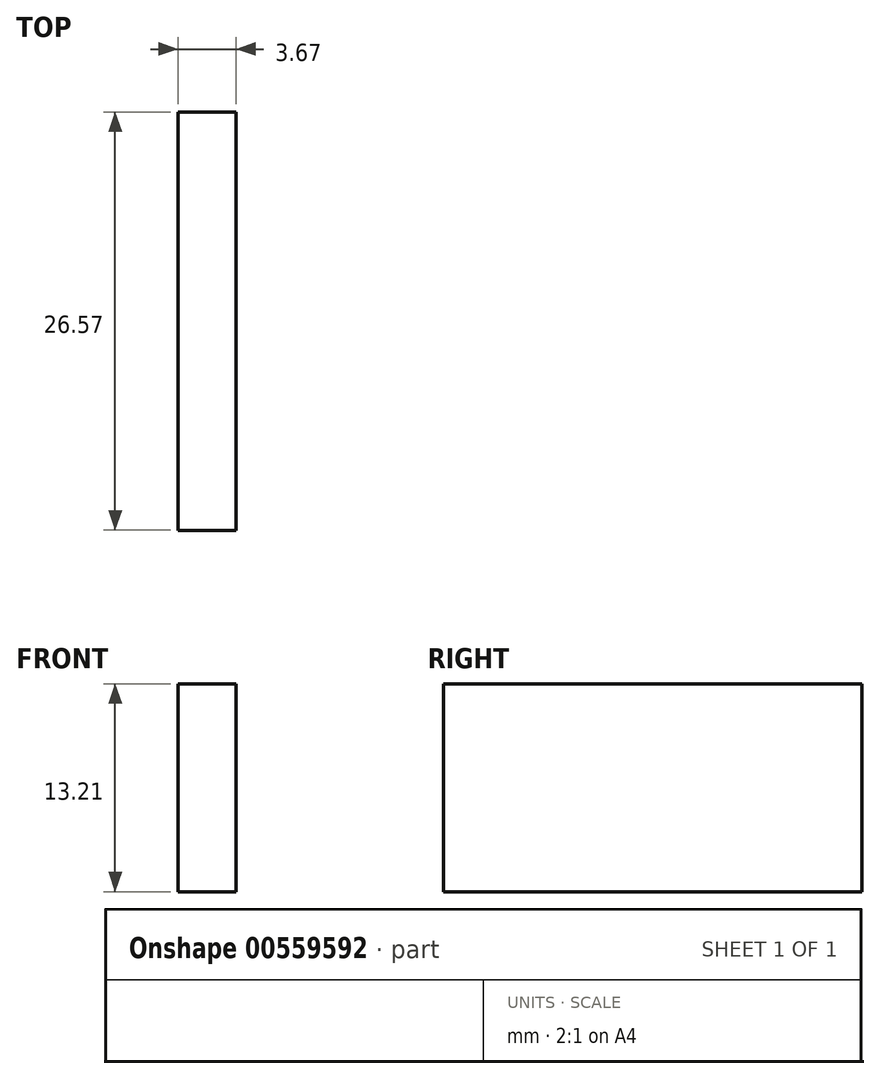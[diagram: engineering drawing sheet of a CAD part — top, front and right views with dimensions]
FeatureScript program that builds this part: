
annotation { "Feature Type Name" : "Feature", "Feature Type Description" : "" }
export const myFeature = defineFeature(function(context is Context, id is Id, definition is map)
    precondition{}
    {
        {
            var Q0;
            Q0=qCreatedBy(makeId("Top.planeOp"),FACE);
            var sketch = newSketch(context, id + "F0", { "sketchPlane" : qUnion([Q0])});
            skLineSegment(sketch, "E0", {"start": v(-37.87, -14.35) * mm, "end": v(-37.87, 12.22) * mm});
            skLineSegment(sketch, "E1", {"start": v(-37.87, 12.22) * mm, "end": v(-34.2, 12.22) * mm});
            skLineSegment(sketch, "E2", {"start": v(-34.2, 12.22) * mm, "end": v(-34.2, -14.35) * mm});
            skLineSegment(sketch, "E3", {"start": v(-34.2, -14.35) * mm, "end": v(-37.87, -14.35) * mm});
            skSolve(sketch);
        }
        {
            var Q0;
            Q0=makeQuery(id+"F0.imprint","IMPRINT",FACE,{"disambiguationData":[TD([[makeQuery(id+"F0.imprint","IMPRINT",EDGE,{"derivedFrom":sQuery(id+"F0.wireOp",EDGE,"E0")}),-1.0]])]});
            extrude(context, id + "F1", {"entities" : qUnion([Q0]), "depth" : 13.2 * mm, "offsetDistance" : 25.4 * mm});
        }
    });
